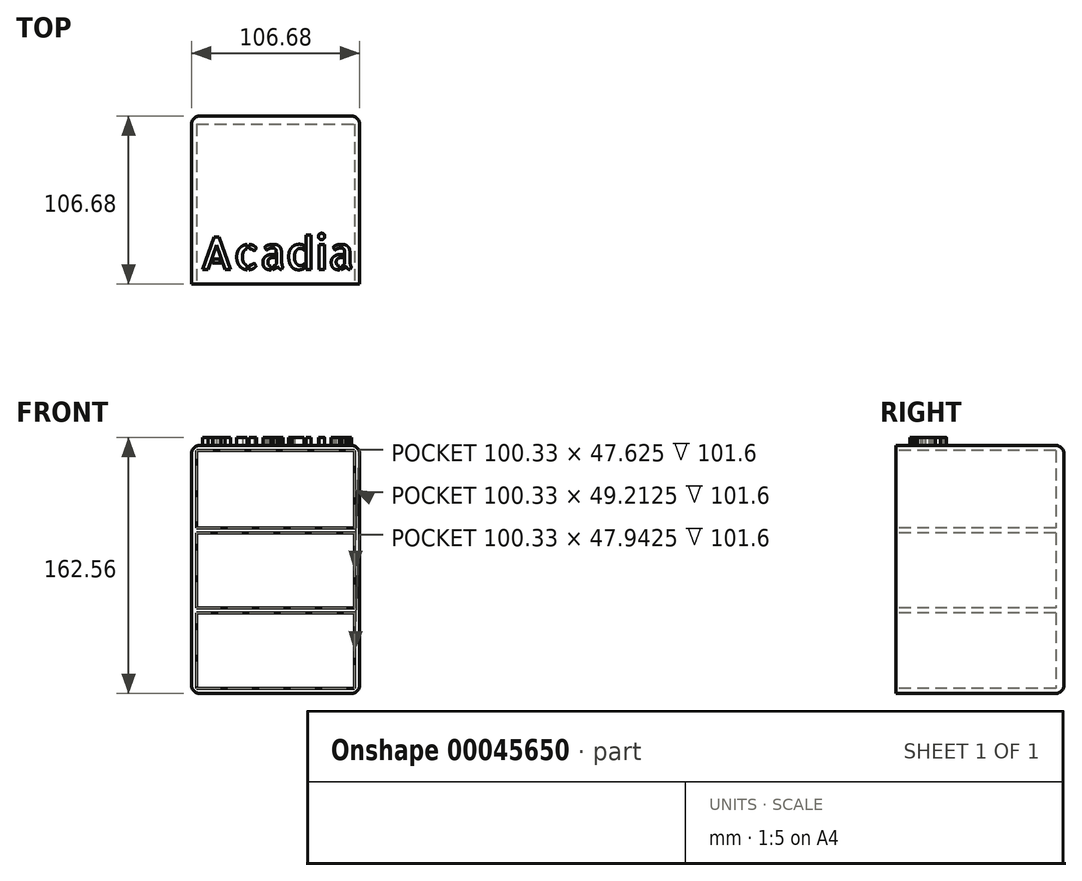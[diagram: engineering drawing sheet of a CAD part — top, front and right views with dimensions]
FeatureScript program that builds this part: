
annotation { "Feature Type Name" : "Feature", "Feature Type Description" : "" }
export const myFeature = defineFeature(function(context is Context, id is Id, definition is map)
    precondition{}
    {
        {
            var Q0;
            Q0=qCreatedBy(makeId("Front.planeOp"),FACE);
            var sketch = newSketch(context, id + "F0", { "sketchPlane" : qUnion([Q0])});
            skLineSegment(sketch, "E0.bottom", {"start": v(-51.12, 110.97) * mm, "end": v(55.56, 110.97) * mm});
            skLineSegment(sketch, "E0.top", {"start": v(-51.12, -46.51) * mm, "end": v(55.56, -46.51) * mm});
            skLineSegment(sketch, "E0.left", {"start": v(-51.12, 110.97) * mm, "end": v(-51.12, -46.51) * mm});
            skLineSegment(sketch, "E0.right", {"start": v(55.56, 110.97) * mm, "end": v(55.56, -46.51) * mm});
            skSolve(sketch);
        }
        {
            var Q0;
            Q0=qSketchRegion(id+"F0",true);
            extrude(context, id + "F1", {"entities" : qUnion([Q0]), "depth" : 106.68 * mm});
        }
        {
            var Q0;
            Q0=makeQuery(id+"F1.opExtrude","CAP_FACE",FACE,{"disambiguationData":[OSD([sQuery(id+"F0.wireOp",EDGE,"E0.bottom"),sQuery(id+"F0.wireOp",EDGE,"E0.top"),sQuery(id+"F0.wireOp",EDGE,"E0.left"),sQuery(id+"F0.wireOp",EDGE,"E0.right")])],"isStart":false});
            var sketch = newSketch(context, id + "F2", { "sketchPlane" : qUnion([Q0])});
            skLineSegment(sketch, "E1.bottom", {"start": v(-47.94, 107.8) * mm, "end": v(52.39, 107.8) * mm});
            skLineSegment(sketch, "E1.top", {"start": v(-47.94, -43.34) * mm, "end": v(52.39, -43.34) * mm});
            skLineSegment(sketch, "E1.left", {"start": v(-47.94, 107.8) * mm, "end": v(-47.94, -43.34) * mm});
            skLineSegment(sketch, "E1.right", {"start": v(52.39, 107.8) * mm, "end": v(52.39, -43.34) * mm});
            skSolve(sketch);
        }
        {
            var Q0;
            Q0=qSketchRegion(id+"F2",true);
            extrude(context, id + "F3", {"entities" : qUnion([Q0]), "operationType" : NewBodyOperationType.REMOVE, "oppositeDirection" : true, "depth" : 101.6 * mm});
        }
        {
            var Q0;
            Q0=makeQuery(id+"F1.opExtrude","CAP_FACE",FACE,{"disambiguationData":[OSD([sQuery(id+"F0.wireOp",EDGE,"E0.bottom"),sQuery(id+"F0.wireOp",EDGE,"E0.top"),sQuery(id+"F0.wireOp",EDGE,"E0.left"),sQuery(id+"F0.wireOp",EDGE,"E0.right")])],"isStart":false});
            var sketch = newSketch(context, id + "F4", { "sketchPlane" : qUnion([Q0])});
            skLineSegment(sketch, "E2.bottom", {"start": v(-51.12, 55.4) * mm, "end": v(55.56, 55.4) * mm});
            skLineSegment(sketch, "E2.top", {"start": v(-51.12, 58.58) * mm, "end": v(55.56, 58.58) * mm});
            skLineSegment(sketch, "E2.left", {"start": v(-51.12, 58.58) * mm, "end": v(-51.12, 55.4) * mm});
            skLineSegment(sketch, "E2.right", {"start": v(55.56, 58.58) * mm, "end": v(55.56, 55.4) * mm});
            skLineSegment(sketch, "E3.bottom", {"start": v(-51.12, 7.78) * mm, "end": v(55.56, 7.78) * mm});
            skLineSegment(sketch, "E3.top", {"start": v(-51.12, 4.6) * mm, "end": v(55.56, 4.6) * mm});
            skLineSegment(sketch, "E3.left", {"start": v(-51.12, 7.78) * mm, "end": v(-51.12, 4.6) * mm});
            skLineSegment(sketch, "E3.right", {"start": v(55.56, 7.78) * mm, "end": v(55.56, 4.6) * mm});
            skLineSegment(sketch, "E4", {"start": v(55.56, 6.2) * mm, "end": v(-51.12, 6.2) * mm});
            skLineSegment(sketch, "E5", {"start": v(-51.12, 57) * mm, "end": v(55.56, 57) * mm});
            skSolve(sketch);
        }
        {
            var Q0;
            Q0=qSketchRegion(id+"F4",true);
            extrude(context, id + "F5", {"entities" : qUnion([Q0]), "operationType" : NewBodyOperationType.ADD, "oppositeDirection" : true, "depth" : 101.6 * mm});
        }
        {
            var Q0;
            Q0=makeQuery(id+"F1.opExtrude","SWEPT_EDGE",EDGE,{"disambiguationData":[OSD([sQuery(id+"F0.wireOp",EDGE,"E0.bottom"),sQuery(id+"F0.wireOp",EDGE,"E0.right")])]});
            var Q1;
            Q1=makeQuery(id+"F1.opExtrude","SWEPT_EDGE",EDGE,{"disambiguationData":[OSD([sQuery(id+"F0.wireOp",EDGE,"E0.bottom"),sQuery(id+"F0.wireOp",EDGE,"E0.left")])]});
            var Q2;
            Q2=makeQuery(id+"F1.opExtrude","SWEPT_EDGE",EDGE,{"disambiguationData":[OSD([sQuery(id+"F0.wireOp",EDGE,"E0.top"),sQuery(id+"F0.wireOp",EDGE,"E0.right")])]});
            var Q3;
            Q3=makeQuery(id+"F1.opExtrude","SWEPT_EDGE",EDGE,{"disambiguationData":[OSD([sQuery(id+"F0.wireOp",EDGE,"E0.top"),sQuery(id+"F0.wireOp",EDGE,"E0.left")])]});
            var Q4;
            Q4=makeQuery(id+"F1.opExtrude","CAP_EDGE",EDGE,{"disambiguationData":[OSD([sQuery(id+"F0.wireOp",EDGE,"E0.left")])],"isStart":true});
            var Q5;
            Q5=makeQuery(id+"F1.opExtrude","CAP_EDGE",EDGE,{"disambiguationData":[OSD([sQuery(id+"F0.wireOp",EDGE,"E0.bottom")])],"isStart":true});
            var Q6;
            Q6=makeQuery(id+"F1.opExtrude","CAP_EDGE",EDGE,{"disambiguationData":[OSD([sQuery(id+"F0.wireOp",EDGE,"E0.right")])],"isStart":true});
            var Q7;
            Q7=makeQuery(id+"F1.opExtrude","CAP_EDGE",EDGE,{"disambiguationData":[OSD([sQuery(id+"F0.wireOp",EDGE,"E0.top")])],"isStart":true});
            fillet(context, id + "F6", {"entities" : qUnion([Q0, Q1, Q2, Q3, Q4, Q5, Q6, Q7]), "radius" : 5.08 * mm, "tangentPropagation" : true, "allowEdgeOverflow" : false});
        }
        {
            var Q0;
            Q0=makeQuery(id+"F1.opExtrude","SWEPT_FACE",FACE,{"disambiguationData":[OSD([sQuery(id+"F0.wireOp",EDGE,"E0.bottom")])]});
            var sketch = newSketch(context, id + "F7", { "sketchPlane" : qUnion([Q0])});
            skText(sketch, "E6", { "text": "Acadia", "fontName": "AllertaStencil-Regular.ttf"});
            const initialGuessF7  = {"E6": [-0.04604, -0.09756, 1, 0, 0.02091]};
            skSetInitialGuess(sketch, initialGuessF7);
            skSolve(sketch);
        }
        {
            var Q0;
            Q0 = qSketchRegion(id + "F7", true);
            extrude(context, id + "F8", {"entities" : qUnion([Q0]), "operationType" : NewBodyOperationType.ADD, "depth" : 5.08 * mm});
        }
    });
